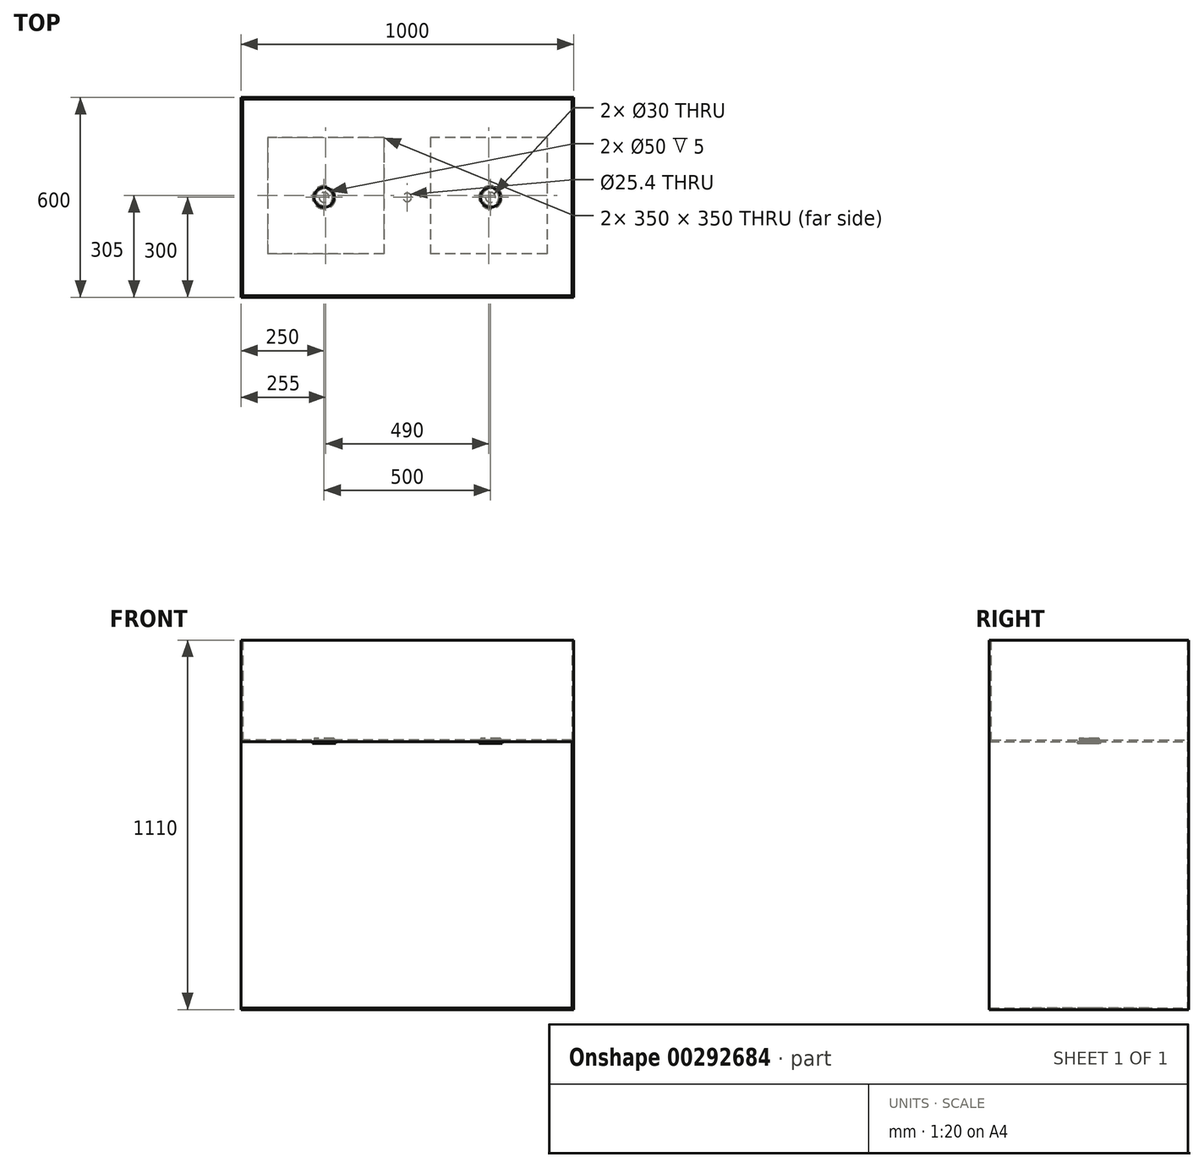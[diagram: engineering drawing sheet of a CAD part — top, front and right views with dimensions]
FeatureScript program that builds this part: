
annotation { "Feature Type Name" : "Feature", "Feature Type Description" : "" }
export const myFeature = defineFeature(function(context is Context, id is Id, definition is map)
    precondition{}
    {
        {
            var Q0;
            Q0=qCreatedBy(makeId("Top.planeOp"),FACE);
            var sketch = newSketch(context, id + "F0", { "sketchPlane" : qUnion([Q0])});
            skLineSegment(sketch, "E0.bottom", {"start": v(500, -300) * mm, "end": v(-500, -300) * mm});
            skLineSegment(sketch, "E0.top", {"start": v(500, 300) * mm, "end": v(-500, 300) * mm});
            skLineSegment(sketch, "E0.left", {"start": v(500, -300) * mm, "end": v(500, 300) * mm});
            skLineSegment(sketch, "E0.right", {"start": v(-500, -300) * mm, "end": v(-500, 300) * mm});
            skCircle(sketch, "E1", {"center": v(250, 0) * mm, "radius": 25 * mm});
            skCircle(sketch, "E2", {"center": v(-250, 0) * mm, "radius": 25 * mm});
            skSolve(sketch);
        }
        {
            var Q0;
            Q0=makeQuery(id+"F0.imprint","IMPRINT",FACE,{"disambiguationData":[TD([[makeQuery(id+"F0.imprint","IMPRINT",EDGE,{"derivedFrom":sQuery(id+"F0.wireOp",EDGE,"E0.bottom")}),-1.0]])]});
            extrude(context, id + "F1", {"entities" : qUnion([Q0]), "depth" : 5 * mm});
        }
        {
            var Q0;
            Q0=qCreatedBy(makeId("Top.planeOp"),FACE);
            var sketch = newSketch(context, id + "F2", { "sketchPlane" : qUnion([Q0])});
            skCircle(sketch, "E3", {"center": v(-250, 0) * mm, "radius": 15 * mm});
            skCircle(sketch, "E4", {"center": v(250, 0) * mm, "radius": 15 * mm});
            skCircle(sketch, "E5", {"center": v(-250, 0) * mm, "radius": 35 * mm});
            skCircle(sketch, "E6", {"center": v(250, 0) * mm, "radius": 35 * mm});
            skSolve(sketch);
        }
        {
            var Q0;
            Q0=makeQuery(id+"F2.imprint","IMPRINT",FACE,{"disambiguationData":[TD([[makeQuery(id+"F2.imprint","IMPRINT",EDGE,{"derivedFrom":sQuery(id+"F2.wireOp",EDGE,"E3")}),-1.0]])]});
            var Q1;
            Q1=makeQuery(id+"F2.imprint","IMPRINT",FACE,{"disambiguationData":[TD([[makeQuery(id+"F2.imprint","IMPRINT",EDGE,{"derivedFrom":sQuery(id+"F2.wireOp",EDGE,"E4")}),-1.0]])]});
            extrude(context, id + "F3", {"entities" : qUnion([Q0, Q1]), "oppositeDirection" : true, "depth" : 5 * mm});
        }
        {
            var Q0;
            Q0=makeQuery(id+"F1.opExtrude","SWEPT_FACE",FACE,{"disambiguationData":[OSD([sQuery(id+"F0.wireOp",EDGE,"E0.top")])]});
            cPlane(context, id + "F4", {"entities" : qUnion([Q0]), "cplaneType" : CPlaneType.OFFSET, "offset" : 0 * mm, "width" : 150 * mm, "height" : 150 * mm});
        }
        {
            var Q0;
            Q0=qCreatedBy(id+"F4.planeOp",FACE);
            var sketch = newSketch(context, id + "F5", { "sketchPlane" : qUnion([Q0])});
            skLineSegment(sketch, "E7.bottom", {"start": v(500, 0) * mm, "end": v(-500, 0) * mm});
            skLineSegment(sketch, "E7.top", {"start": v(500, -800) * mm, "end": v(-500, -800) * mm});
            skLineSegment(sketch, "E7.left", {"start": v(500, 0) * mm, "end": v(500, -800) * mm});
            skLineSegment(sketch, "E7.right", {"start": v(-500, 0) * mm, "end": v(-500, -800) * mm});
            skSolve(sketch);
        }
        {
            var Q0;
            Q0=makeQuery(id+"F5.imprint","IMPRINT",FACE,{"disambiguationData":[TD([[makeQuery(id+"F5.imprint","IMPRINT",EDGE,{"derivedFrom":sQuery(id+"F5.wireOp",EDGE,"E7.bottom")}),1.0]])]});
            extrude(context, id + "F6", {"entities" : qUnion([Q0]), "operationType" : NewBodyOperationType.ADD, "oppositeDirection" : true, "depth" : 5 * mm});
        }
        {
            var Q0;
            {var subQ0=sQuery(id+"F5.wireOp",EDGE,"E7.right");Q0=makeQuery(id+"FlKtmnur0S63wQR_4.1.F6.boolean.opBoolean","MERGE",FACE,{"derivedFrom":[makeQuery(id+"F6.boolean.opBoolean","MERGE",FACE,{"derivedFrom":[makeQuery(id+"F1.opExtrude","SWEPT_FACE",FACE,{"disambiguationData":[OSD([sQuery(id+"F0.wireOp",EDGE,"E0.left")])]}),makeQuery(id+"F6.opExtrude","SWEPT_FACE",FACE,{"disambiguationData":[OSD([subQ0])]})]}),makeQuery(id+"FlKtmnur0S63wQR_4.1.F6.opExtrude","SWEPT_FACE",FACE,{"disambiguationData":[OSD([subQ0])]})]});}
            cPlane(context, id + "F7", {"entities" : qUnion([Q0]), "cplaneType" : CPlaneType.OFFSET, "offset" : 0 * mm, "width" : 150 * mm, "height" : 150 * mm});
        }
        {
            var Q0;
            Q0=qCreatedBy(id+"F7.planeOp",FACE);
            var sketch = newSketch(context, id + "F8", { "sketchPlane" : qUnion([Q0])});
            skLineSegment(sketch, "E8.bottom", {"start": v(300, 5) * mm, "end": v(-300, 5) * mm});
            skLineSegment(sketch, "E8.top", {"start": v(300, -800) * mm, "end": v(-300, -800) * mm});
            skLineSegment(sketch, "E8.left", {"start": v(300, 5) * mm, "end": v(300, -800) * mm});
            skLineSegment(sketch, "E8.right", {"start": v(-300, 5) * mm, "end": v(-300, -800) * mm});
            skSolve(sketch);
        }
        {
            var Q0;
            Q0 = qSketchRegion(id + "F8", true);
            extrude(context, id + "F9", {"entities" : qUnion([Q0]), "operationType" : NewBodyOperationType.ADD, "oppositeDirection" : true, "depth" : 5 * mm});
        }
        {
            var Q0;
            {var subQ0=sQuery(id+"F8.wireOp",EDGE,"E8.top");var subQ1=sQuery(id+"F5.wireOp",EDGE,"E7.top");Q0=makeQuery(id+"FuH1vm16cUdqZ6K_4.1.F9.boolean.opBoolean","MERGE",FACE,{"derivedFrom":[makeQuery(id+"F9.boolean.opBoolean","MERGE",FACE,{"derivedFrom":[makeQuery(id+"F6.opExtrude","SWEPT_FACE",FACE,{"disambiguationData":[OSD([subQ1])]}),makeQuery(id+"FlKtmnur0S63wQR_4.1.F6.opExtrude","SWEPT_FACE",FACE,{"disambiguationData":[OSD([subQ1])]}),makeQuery(id+"F9.opExtrude","SWEPT_FACE",FACE,{"disambiguationData":[OSD([subQ0])]})]}),makeQuery(id+"FuH1vm16cUdqZ6K_4.1.F9.opExtrude","SWEPT_FACE",FACE,{"disambiguationData":[OSD([subQ0])]})]});}
            cPlane(context, id + "F10", {"entities" : qUnion([Q0]), "cplaneType" : CPlaneType.OFFSET, "offset" : 0 * mm, "width" : 150 * mm, "height" : 150 * mm});
        }
        {
            var Q0;
            Q0=qCreatedBy(id+"F10.planeOp",FACE);
            var sketch = newSketch(context, id + "F11", { "sketchPlane" : qUnion([Q0])});
            skLineSegment(sketch, "E9.bottom", {"start": v(500, 300) * mm, "end": v(-500, 300) * mm});
            skLineSegment(sketch, "E9.top", {"start": v(500, -300) * mm, "end": v(-500, -300) * mm});
            skLineSegment(sketch, "E9.left", {"start": v(500, 300) * mm, "end": v(500, -300) * mm});
            skLineSegment(sketch, "E9.right", {"start": v(-500, 300) * mm, "end": v(-500, -300) * mm});
            skLineSegment(sketch, "E10.bottom", {"start": v(420, -180) * mm, "end": v(70, -180) * mm});
            skLineSegment(sketch, "E10.top", {"start": v(420, 170) * mm, "end": v(70, 170) * mm});
            skLineSegment(sketch, "E10.left", {"start": v(420, -180) * mm, "end": v(420, 170) * mm});
            skLineSegment(sketch, "E10.right", {"start": v(70, -180) * mm, "end": v(70, 170) * mm});
            skLineSegment(sketch, "E11.bottom", {"start": v(-70, -180) * mm, "end": v(-420, -180) * mm});
            skLineSegment(sketch, "E11.top", {"start": v(-70, 170) * mm, "end": v(-420, 170) * mm});
            skLineSegment(sketch, "E11.left", {"start": v(-70, -180) * mm, "end": v(-70, 170) * mm});
            skLineSegment(sketch, "E11.right", {"start": v(-420, -180) * mm, "end": v(-420, 170) * mm});
            skCircle(sketch, "E12", {"center": v(0, 0) * mm, "radius": 12.7 * mm});
            skSolve(sketch);
        }
        {
            var Q0;
            Q0 = qSketchRegion(id + "F11", true);
            extrude(context, id + "F12", {"entities" : qUnion([Q0]), "operationType" : NewBodyOperationType.ADD, "depth" : 5 * mm});
        }
        {
            var Q0;
            Q0=makeQuery(id+"F1.opExtrude","CAP_FACE",FACE,{"disambiguationData":[OSD([sQuery(id+"F0.wireOp",EDGE,"E0.bottom"),sQuery(id+"F0.wireOp",EDGE,"E0.top"),sQuery(id+"F0.wireOp",EDGE,"E0.left"),sQuery(id+"F0.wireOp",EDGE,"E0.right"),sQuery(id+"F0.wireOp",EDGE,"E1"),sQuery(id+"F0.wireOp",EDGE,"E2")])],"isStart":false});
            var sketch = newSketch(context, id + "F13", { "sketchPlane" : qUnion([Q0])});
            skLineSegment(sketch, "E13.bottom", {"start": v(500, -300) * mm, "end": v(-500, -300) * mm});
            skLineSegment(sketch, "E13.top", {"start": v(500, 300) * mm, "end": v(-500, 300) * mm});
            skLineSegment(sketch, "E13.left", {"start": v(500, -300) * mm, "end": v(500, 300) * mm});
            skLineSegment(sketch, "E13.right", {"start": v(-500, -300) * mm, "end": v(-500, 300) * mm});
            skPoint(sketch, "E13.middle", {"position": v(0, 0) * mm});
            skSolve(sketch);
        }
        {
            var Q0;
            Q0 = qSketchRegion(id + "F13", true);
            extrude(context, id + "F14", {"entities" : qUnion([Q0]), "operationType" : NewBodyOperationType.ADD, "depth" : 300 * mm});
        }
        {
            var Q0;
            Q0=makeQuery(id+"F14.opExtrude","CAP_FACE",FACE,{"disambiguationData":[OSD([sQuery(id+"F13.wireOp",EDGE,"E13.bottom"),sQuery(id+"F13.wireOp",EDGE,"E13.top"),sQuery(id+"F13.wireOp",EDGE,"E13.left"),sQuery(id+"F13.wireOp",EDGE,"E13.right")])],"isStart":false});
            shell(context, id + "F15", {"entities" : qUnion([Q0]), "thickness" : 5 * mm});
        }
    });
